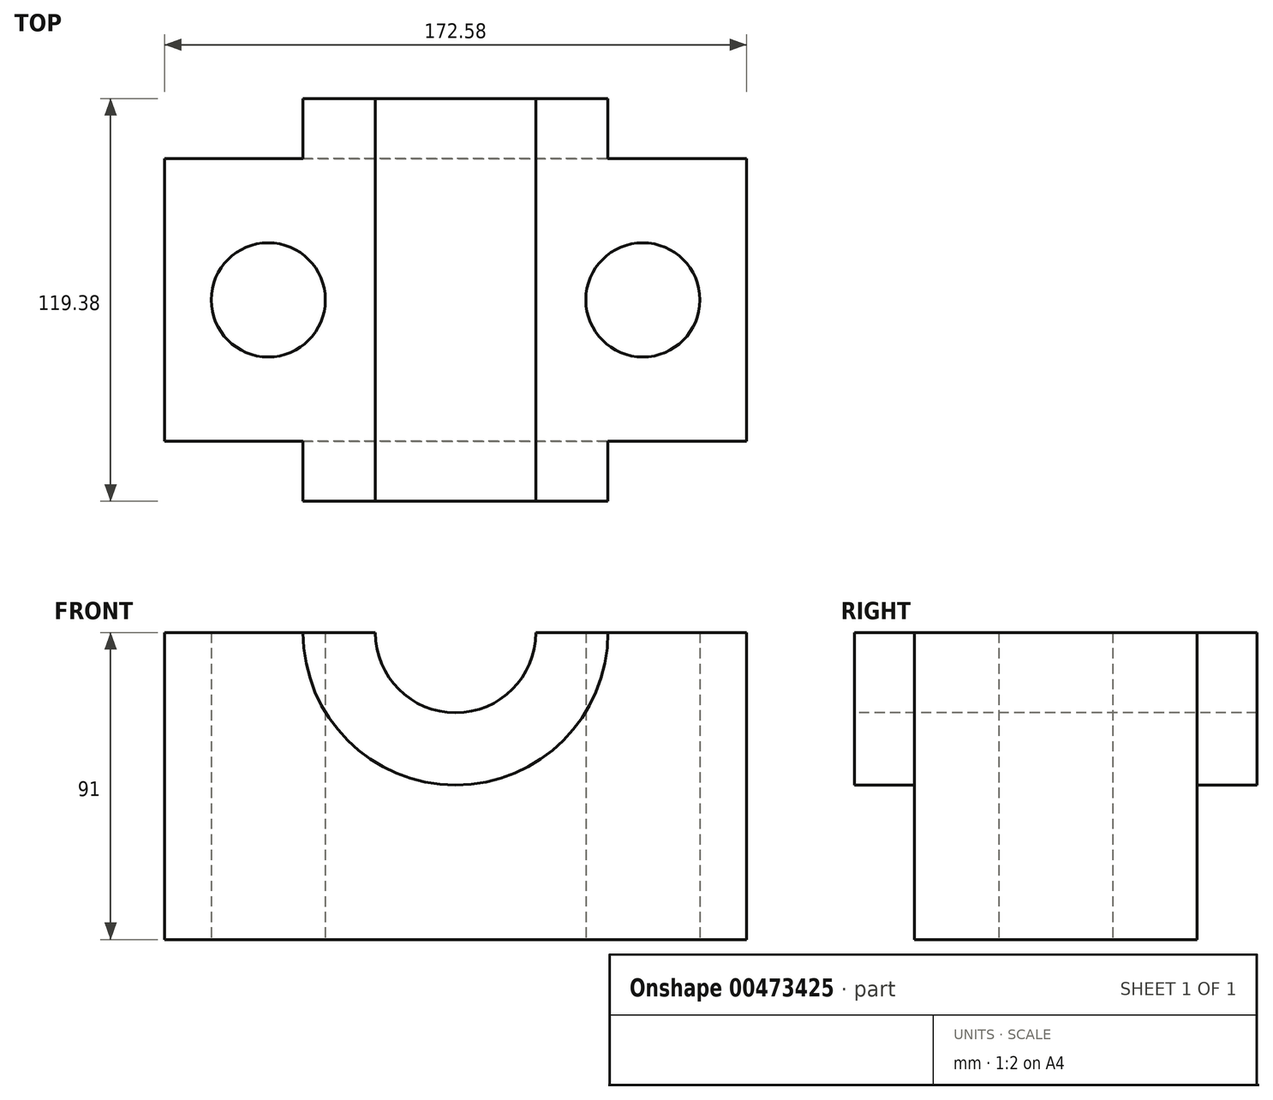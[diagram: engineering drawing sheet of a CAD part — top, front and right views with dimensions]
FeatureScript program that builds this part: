
annotation { "Feature Type Name" : "Feature", "Feature Type Description" : "" }
export const myFeature = defineFeature(function(context is Context, id is Id, definition is map)
    precondition{}
    {
        {
            var Q0;
            Q0=qCreatedBy(makeId("Front.planeOp"),FACE);
            var sketch = newSketch(context, id + "F0", { "sketchPlane" : qUnion([Q0])});
            skLineSegment(sketch, "E0.bottom", {"start": v(86.29, -45.5) * mm, "end": v(-86.29, -45.5) * mm});
            skLineSegment(sketch, "E0.top", {"start": v(86.29, 45.5) * mm, "end": v(23.77, 45.5) * mm});
            skLineSegment(sketch, "E0.left", {"start": v(86.29, -45.5) * mm, "end": v(86.29, 45.5) * mm});
            skLineSegment(sketch, "E0.right", {"start": v(-86.29, -45.5) * mm, "end": v(-86.29, 45.5) * mm});
            skPoint(sketch, "E0.middle", {"position": v(0, 0) * mm});
            skArc(sketch, "E1", {"start": v(-45.2, 45.5) * mm, "mid": v(0, 0.3) * mm, "end": v(45.2, 45.5) * mm});
            skArc(sketch, "E2", {"start": v(-23.77, 45.5) * mm, "mid": v(0, 21.73) * mm, "end": v(23.77, 45.5) * mm});
            skLineSegment(sketch, "E3.trimOffspring", {"start": v(-23.77, 45.5) * mm, "end": v(-86.29, 45.5) * mm});
            skSolve(sketch);
        }
        {
            var Q0;
            Q0=makeQuery(id+"F0.imprint","IMPRINT",FACE,{"disambiguationData":[TD([[makeQuery(id+"F0.imprint","IMPRINT",EDGE,{"derivedFrom":sQuery(id+"F0.wireOp",EDGE,"E0.bottom")}),-1.0]])]});
            extrude(context, id + "F1", {"entities" : qUnion([Q0]), "oppositeDirection" : true, "depth" : 83.82 * mm});
        }
        {
            var Q0;
            {var subQ2=sQuery(id+"F0.wireOp",EDGE,"E1");Q0=makeQuery(id+"F0.imprint","IMPRINT",FACE,{"disambiguationData":[TD([[makeQuery(id+"F0.imprint","IMPRINT",EDGE,{"derivedFrom":subQ2}),1.0]])]});}
            extrude(context, id + "F2", {"entities" : qUnion([Q0]), "operationType" : NewBodyOperationType.ADD, "oppositeDirection" : true, "depth" : 101.6 * mm, "hasSecondDirection" : true, "secondDirectionOppositeDirection" : false, "secondDirectionDepth" : 17.78 * mm});
        }
        {
            var Q0;
            {var subQ0=sQuery(id+"F0.wireOp",EDGE,"E3.trimOffspring");Q0=makeQuery(id+"F2.boolean.opBoolean","MERGE",FACE,{"derivedFrom":[makeQuery(id+"F1.opExtrude","SWEPT_FACE",FACE,{"disambiguationData":[OSD([subQ0])]}),makeQuery(id+"F2.opExtrude","SWEPT_FACE",FACE,{"disambiguationData":[OSD([subQ0])]})]});}
            var sketch = newSketch(context, id + "F3", { "sketchPlane" : qUnion([Q0])});
            skLineSegment(sketch, "E4", {"start": v(-86.29, 41.91) * mm, "end": v(86.63, 41.91) * mm});
            skPoint(sketch, "E4.endSnap0", {"position": v(-86.29, 41.91) * mm});
            skPoint(sketch, "E5", {"position": v(-55.54, 41.91) * mm});
            skCircle(sketch, "E6", {"center": v(-55.54, 41.91) * mm, "radius": 16.93 * mm});
            skCircle(sketch, "E7.MirrorC", {"center": v(55.54, 41.91) * mm, "radius": 16.93 * mm});
            skSolve(sketch);
        }
        {
            var Q0;
            Q0 = qSketchRegion(id + "F3", true);
            extrude(context, id + "F4", {"entities" : qUnion([Q0]), "operationType" : NewBodyOperationType.REMOVE, "endBound" : BoundingType.SYMMETRIC, "depth" : 352.04 * mm});
        }
    });
